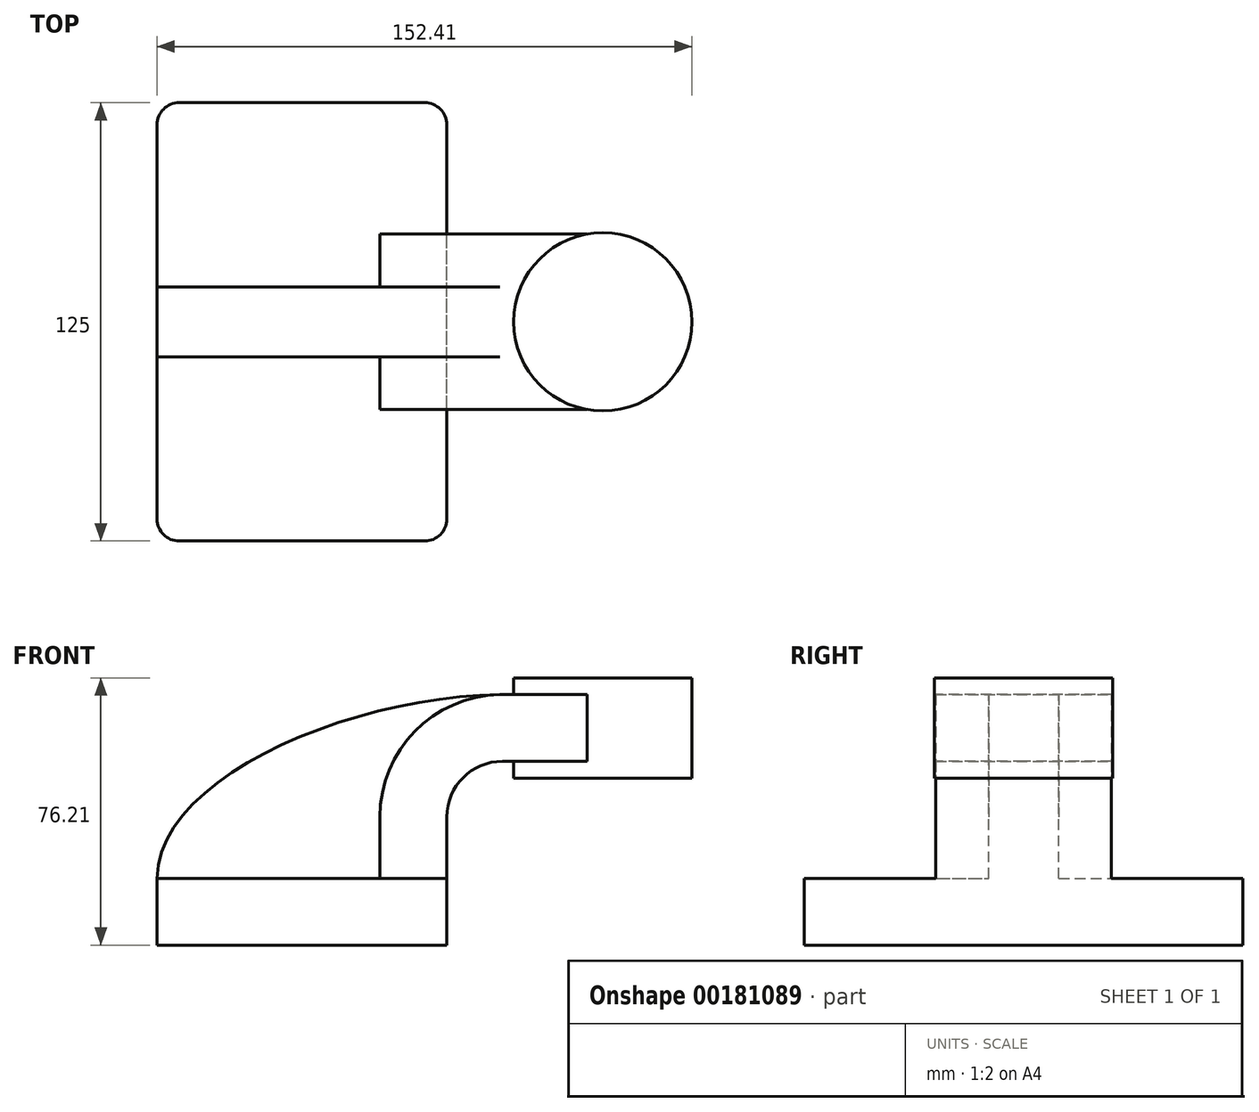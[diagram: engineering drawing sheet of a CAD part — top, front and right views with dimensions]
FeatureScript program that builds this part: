
annotation { "Feature Type Name" : "Feature", "Feature Type Description" : "" }
export const myFeature = defineFeature(function(context is Context, id is Id, definition is map)
    precondition{}
    {
        {
            var Q0;
            Q0=qCreatedBy(makeId("Front.planeOp"),FACE);
            var sketch = newSketch(context, id + "F0", { "sketchPlane" : qUnion([Q0])});
            skLineSegment(sketch, "E0.bottom", {"start": v(-41.27, 9.52) * mm, "end": v(41.27, 9.53) * mm});
            skLineSegment(sketch, "E0.top", {"start": v(-41.27, -9.53) * mm, "end": v(41.27, -9.53) * mm});
            skLineSegment(sketch, "E0.left", {"start": v(-41.27, 9.52) * mm, "end": v(-41.27, -9.53) * mm});
            skLineSegment(sketch, "E0.right", {"start": v(41.27, 9.53) * mm, "end": v(41.27, -9.52) * mm});
            skPoint(sketch, "E0.middle", {"position": v(0, 0) * mm});
            skLineSegment(sketch, "E1.bottom", {"start": v(60.32, 66.68) * mm, "end": v(111.12, 66.68) * mm});
            skLineSegment(sketch, "E1.top", {"start": v(60.33, 38.1) * mm, "end": v(111.12, 38.1) * mm});
            skLineSegment(sketch, "E1.left", {"start": v(60.32, 66.67) * mm, "end": v(60.33, 38.1) * mm});
            skLineSegment(sketch, "E1.right", {"start": v(111.12, 66.67) * mm, "end": v(111.12, 38.1) * mm});
            skPoint(sketch, "E1.middle", {"position": v(85.72, 52.39) * mm});
            skLineSegment(sketch, "E2", {"start": v(41.27, 9.53) * mm, "end": v(41.27, 27) * mm});
            skArc(sketch, "E3", {"start": v(41.27, 27) * mm, "mid": v(45.92, 38.23) * mm, "end": v(57.15, 42.88) * mm});
            skLineSegment(sketch, "E4", {"start": v(57.15, 42.88) * mm, "end": v(85.72, 42.88) * mm});
            skLineSegment(sketch, "E5.0", {"start": v(57.15, 61.92) * mm, "end": v(85.72, 61.92) * mm});
            skArc(sketch, "E5.1", {"start": v(22.22, 27) * mm, "mid": v(32.45, 51.7) * mm, "end": v(57.15, 61.92) * mm});
            skLineSegment(sketch, "E5.2", {"start": v(22.22, 9.53) * mm, "end": v(22.22, 27) * mm});
            skLineSegment(sketch, "E6", {"start": v(85.72, 38.1) * mm, "end": v(85.72, 66.68) * mm});
            skFitSpline(sketch, "E7", {"points": [v(-41.27, 9.52) * mm, v(57.15, 61.92) * mm], "startDerivative": vector(0.7, 87.37) * mm, "endDerivative": vector(127.64, 1.1) * mm});
            skSolve(sketch);
        }
        {
            var Q0;
            Q0=makeQuery(id+"F0.imprint","IMPRINT",FACE,{"disambiguationData":[TD([[makeQuery(id+"F0.imprint","IMPRINT",EDGE,{"derivedFrom":sQuery(id+"F0.wireOp",EDGE,"E0.top")}),1.0]])]});
            extrude(context, id + "F1", {"entities" : qUnion([Q0]), "endBound" : BoundingType.SYMMETRIC, "depth" : 125 * mm});
        }
        {
            var Q0;
            {var subQ1=sQuery(id+"F0.wireOp",EDGE,"E2");Q0=makeQuery(id+"F0.imprint","IMPRINT",FACE,{"disambiguationData":[TD([[makeQuery(id+"F0.imprint","IMPRINT",EDGE,{"derivedFrom":subQ1}),1.0]])]});}
            extrude(context, id + "F2", {"entities" : qUnion([Q0]), "operationType" : NewBodyOperationType.ADD, "endBound" : BoundingType.SYMMETRIC, "depth" : 50 * mm});
        }
        {
            var Q0;
            {var subQ3=sQuery(id+"F0.wireOp",EDGE,"E5.2");Q0=makeQuery(id+"F0.imprint","IMPRINT",FACE,{"disambiguationData":[TD([[makeQuery(id+"F0.imprint","IMPRINT",EDGE,{"derivedFrom":subQ3}),1.0]])]});}
            extrude(context, id + "F3", {"entities" : qUnion([Q0]), "operationType" : NewBodyOperationType.ADD, "endBound" : BoundingType.SYMMETRIC, "depth" : 20 * mm});
        }
        {
            var Q0;
            {var subQ0=sQuery(id+"F0.wireOp",EDGE,"E5.0");var subQ1=sQuery(id+"F0.wireOp",EDGE,"E1.left");var subQ2=makeQuery(id+"F0.imprint","INTERSECT",VERTEX,{"derivedFrom":[subQ1,subQ0]});Q0=makeQuery(id+"F0.imprint","IMPRINT",FACE,{"disambiguationData":[TD([[makeQuery(id+"F0.imprint","IMPRINT",EDGE,{"disambiguationData":[TD([[subQ2,-1.0]])],"derivedFrom":subQ1}),1.0]])]});}
            extrude(context, id + "F4", {"entities" : qUnion([Q0]), "operationType" : NewBodyOperationType.ADD, "endBound" : BoundingType.SYMMETRIC, "depth" : 50 * mm});
        }
        {
            var Q0;
            {var subQ0=sQuery(id+"F0.wireOp",EDGE,"E1.right");Q0=makeQuery(id+"F0.imprint","IMPRINT",FACE,{"disambiguationData":[TD([[makeQuery(id+"F0.imprint","IMPRINT",EDGE,{"derivedFrom":subQ0}),-1.0]])]});}
            var Q1;
            Q1=sQuery(id+"F0.wireOp",EDGE,"E6");
            revolve(context, id + "F5", {"operationType" : NewBodyOperationType.ADD, "entities" : qUnion([Q0]), "axis" : qUnion([Q1]), "revolveType" : RevolveType.FULL});
        }
        {
            var Q0;
            Q0=makeQuery(id+"F1.opExtrude","CAP_EDGE",EDGE,{"disambiguationData":[OSD([sQuery(id+"F0.wireOp",EDGE,"E0.right")])],"isStart":false});
            var Q1;
            Q1=makeQuery(id+"F1.opExtrude","CAP_EDGE",EDGE,{"disambiguationData":[OSD([sQuery(id+"F0.wireOp",EDGE,"E0.left")])],"isStart":false});
            var Q2;
            Q2=makeQuery(id+"F1.opExtrude","CAP_EDGE",EDGE,{"disambiguationData":[OSD([sQuery(id+"F0.wireOp",EDGE,"E0.right")])],"isStart":true});
            var Q3;
            Q3=makeQuery(id+"F1.opExtrude","CAP_EDGE",EDGE,{"disambiguationData":[OSD([sQuery(id+"F0.wireOp",EDGE,"E0.left")])],"isStart":true});
            fillet(context, id + "F6", {"entities" : qUnion([Q0, Q1, Q2, Q3]), "radius" : 6.3 * mm, "tangentPropagation" : true, "allowEdgeOverflow" : false});
        }
    });
